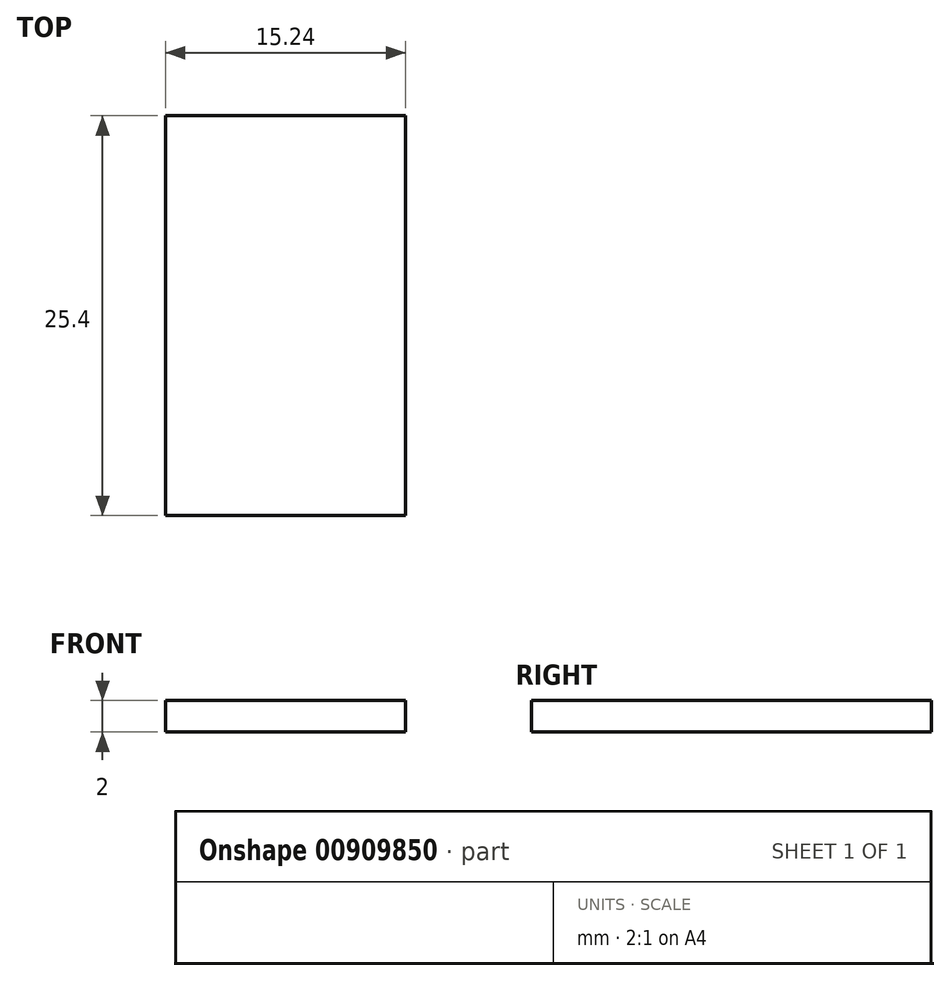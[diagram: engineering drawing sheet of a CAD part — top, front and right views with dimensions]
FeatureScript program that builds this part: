
annotation { "Feature Type Name" : "Feature", "Feature Type Description" : "" }
export const myFeature = defineFeature(function(context is Context, id is Id, definition is map)
    precondition{}
    {
        {
            var Q0;
            Q0=qCreatedBy(makeId("Top.planeOp"),FACE);
            var sketch = newSketch(context, id + "F0", { "sketchPlane" : qUnion([Q0])});
            skLineSegment(sketch, "E0.bottom", {"start": v(7.62, -12.7) * mm, "end": v(-7.62, -12.7) * mm});
            skLineSegment(sketch, "E0.top", {"start": v(7.62, 12.7) * mm, "end": v(-7.62, 12.7) * mm});
            skLineSegment(sketch, "E0.left", {"start": v(7.62, -12.7) * mm, "end": v(7.62, 12.7) * mm});
            skLineSegment(sketch, "E0.right", {"start": v(-7.62, -12.7) * mm, "end": v(-7.62, 12.7) * mm});
            skPoint(sketch, "E0.middle", {"position": v(0, 0) * mm});
            skSolve(sketch);
        }
        {
            var Q0;
            Q0=qSketchRegion(id+"F0",true);
            extrude(context, id + "F1", {"entities" : qUnion([Q0]), "depth" : 2 * mm, "offsetDistance" : 25 * mm});
        }
        {
            var Q0;
            Q0=makeQuery(id+"F1.opExtrude","CAP_FACE",FACE,{"disambiguationData":[OSD([sQuery(id+"F0.wireOp",EDGE,"E0.bottom"),sQuery(id+"F0.wireOp",EDGE,"E0.top"),sQuery(id+"F0.wireOp",EDGE,"E0.left"),sQuery(id+"F0.wireOp",EDGE,"E0.right")])],"isStart":false});
            var sketch = newSketch(context, id + "F2", { "sketchPlane" : qUnion([Q0])});
            skCircle(sketch, "E1", {"center": v(-16, -7.5) * mm, "radius": 1.55 * mm});
            skCircle(sketch, "E2", {"center": v(-16, 7.5) * mm, "radius": 1.55 * mm});
            skCircle(sketch, "E3", {"center": v(16, 7.5) * mm, "radius": 1.55 * mm});
            skCircle(sketch, "E4", {"center": v(16, -7.5) * mm, "radius": 1.55 * mm});
            skLineSegment(sketch, "E5.bottom", {"start": v(-16, 7.5) * mm, "end": v(16, 7.5) * mm, "construction": true});
            skLineSegment(sketch, "E5.top", {"start": v(-16, -7.5) * mm, "end": v(16, -7.5) * mm, "construction": true});
            skLineSegment(sketch, "E5.left", {"start": v(-16, 7.5) * mm, "end": v(-16, -7.5) * mm, "construction": true});
            skLineSegment(sketch, "E5.right", {"start": v(16, 7.5) * mm, "end": v(16, -7.5) * mm, "construction": true});
            skSolve(sketch);
        }
        {
            var Q0;
            Q0=qSketchRegion(id+"F2",true);
            extrude(context, id + "F3", {"entities" : qUnion([Q0]), "operationType" : NewBodyOperationType.REMOVE, "oppositeDirection" : true, "depth" : 25 * mm, "offsetDistance" : 25 * mm});
        }
    });
